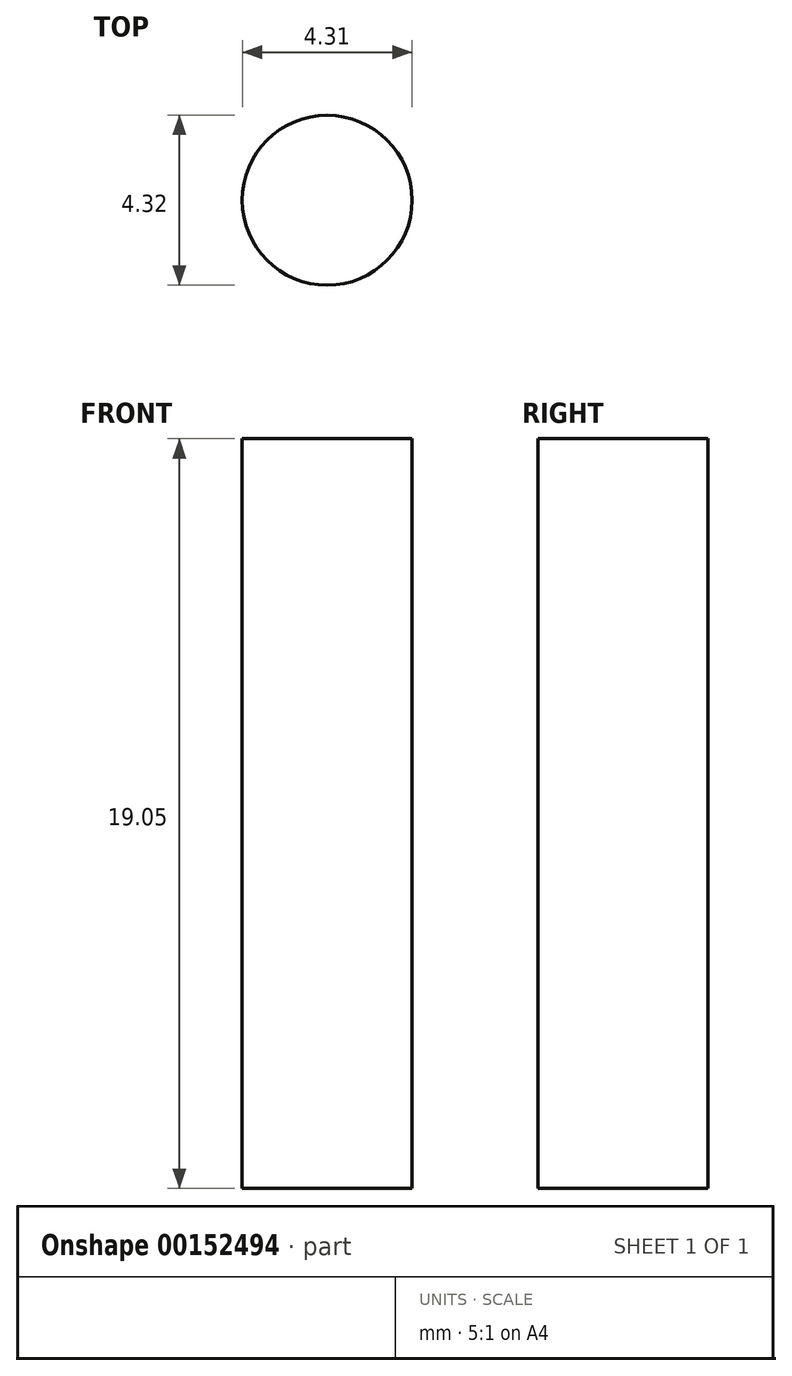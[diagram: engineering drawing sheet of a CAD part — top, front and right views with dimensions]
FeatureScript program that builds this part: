
annotation { "Feature Type Name" : "Feature", "Feature Type Description" : "" }
export const myFeature = defineFeature(function(context is Context, id is Id, definition is map)
    precondition{}
    {
        {
            var Q0;
            Q0=qCreatedBy(makeId("Top.planeOp"),FACE);
            var sketch = newSketch(context, id + "F0", { "sketchPlane" : qUnion([Q0])});
            skCircle(sketch, "E0", {"center": v(-5.4, -3.15) * mm, "radius": 2.16 * mm});
            skSolve(sketch);
        }
        {
            var Q0;
            Q0=makeQuery(id+"F0.imprint","IMPRINT",FACE,{"disambiguationData":[TD([[makeQuery(id+"F0.imprint","IMPRINT",EDGE,{"derivedFrom":sQuery(id+"F0.wireOp",EDGE,"E0")}),1.0]])]});
            extrude(context, id + "F1", {"entities" : qUnion([Q0]), "depth" : 19.05 * mm});
        }
    });
